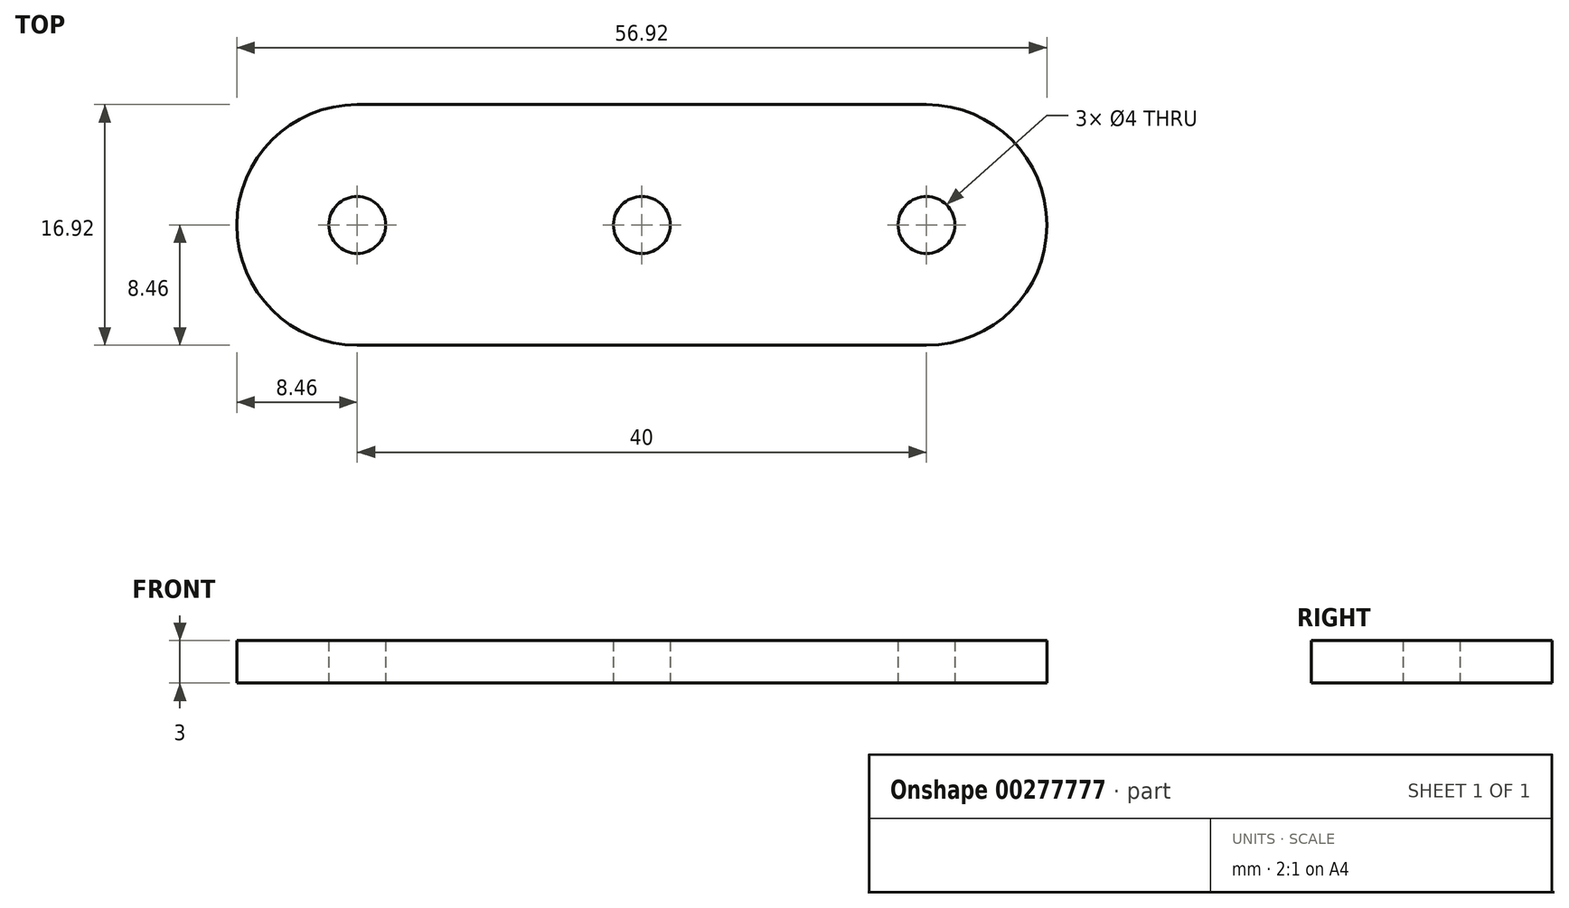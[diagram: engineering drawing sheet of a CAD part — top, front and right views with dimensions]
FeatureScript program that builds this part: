
annotation { "Feature Type Name" : "Feature", "Feature Type Description" : "" }
export const myFeature = defineFeature(function(context is Context, id is Id, definition is map)
    precondition{}
    {
        {
            var Q0;
            Q0=qCreatedBy(makeId("Top.planeOp"),FACE);
            var sketch = newSketch(context, id + "F0", { "sketchPlane" : qUnion([Q0])});
            skLineSegment(sketch, "E0.bottom", {"start": v(-20, 8.46) * mm, "end": v(20, 8.46) * mm});
            skLineSegment(sketch, "E0.top", {"start": v(-20, -8.46) * mm, "end": v(20, -8.46) * mm});
            skPoint(sketch, "E0.middle", {"position": v(0, 0) * mm});
            skArc(sketch, "E1", {"start": v(-20, 8.46) * mm, "mid": v(-28.46, 0) * mm, "end": v(-20, -8.46) * mm});
            skPoint(sketch, "E0.left.start.orphan", {"position": v(-30.46, 8.46) * mm});
            skPoint(sketch, "E2.orphan", {"position": v(-30.46, -8.46) * mm});
            skArc(sketch, "E3.MirrorC", {"start": v(20, 8.46) * mm, "mid": v(28.46, 0) * mm, "end": v(20, -8.46) * mm});
            skPoint(sketch, "E0.right.start.orphan", {"position": v(30.46, 8.46) * mm});
            skPoint(sketch, "E4.orphan", {"position": v(30.46, -8.46) * mm});
            skCircle(sketch, "E5", {"center": v(-20, 0) * mm, "radius": 2 * mm});
            skCircle(sketch, "E6.MirrorC", {"center": v(20, 0) * mm, "radius": 2 * mm});
            skCircle(sketch, "E7", {"center": v(0, 0) * mm, "radius": 2 * mm});
            skSolve(sketch);
        }
        {
            var Q0;
            Q0 = qSketchRegion(id + "F0", true);
            extrude(context, id + "F1", {"entities" : qUnion([Q0]), "depth" : 3 * mm});
        }
    });
